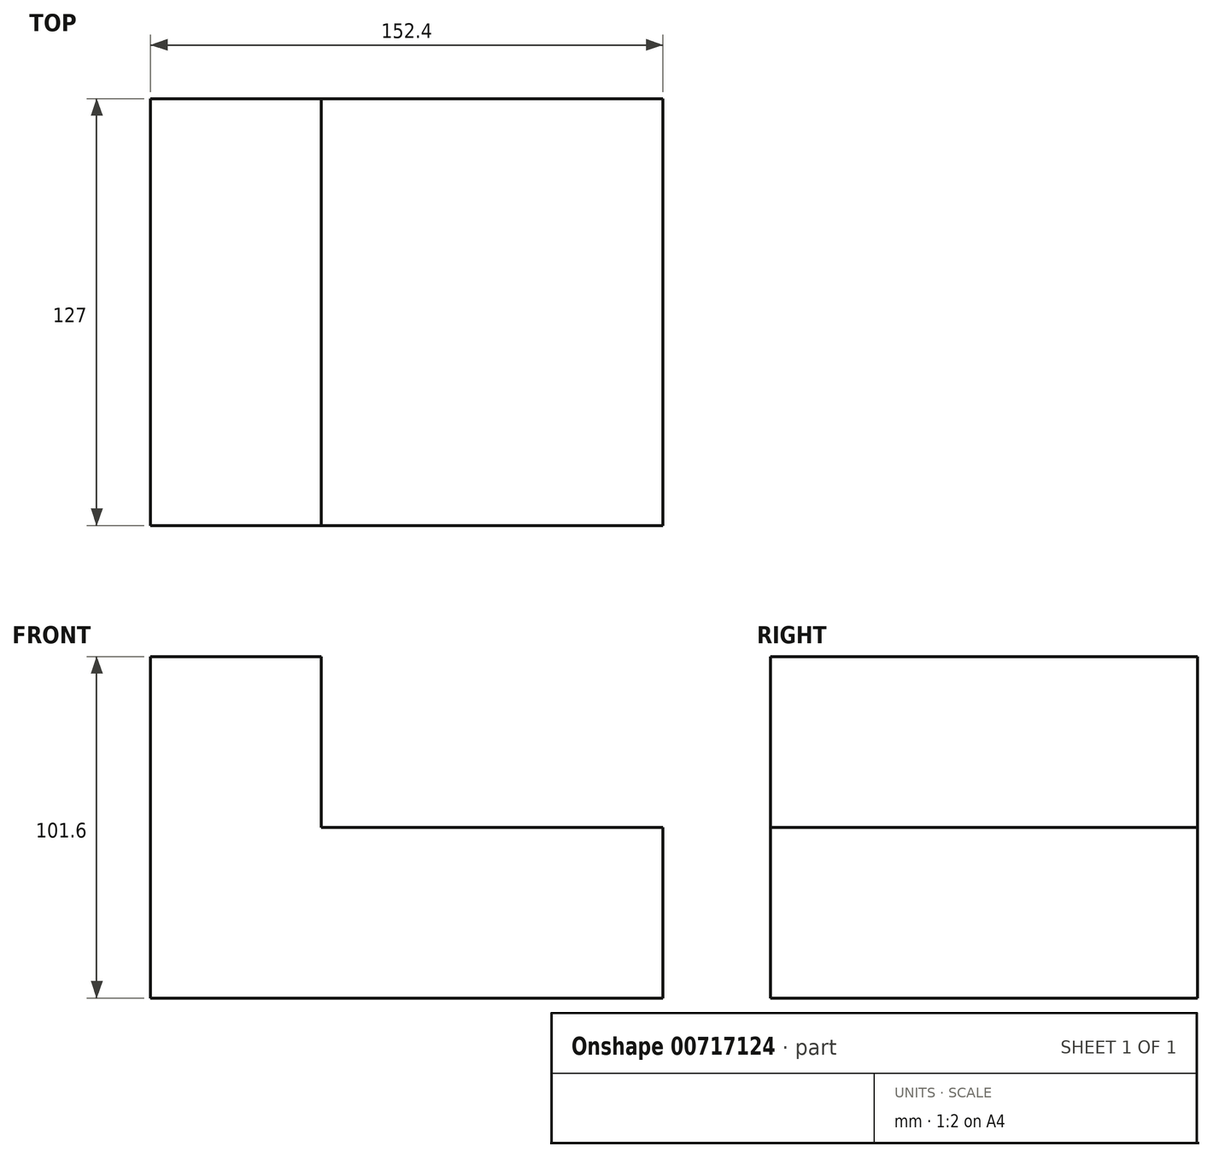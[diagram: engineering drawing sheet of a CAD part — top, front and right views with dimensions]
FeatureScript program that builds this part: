
annotation { "Feature Type Name" : "Feature", "Feature Type Description" : "" }
export const myFeature = defineFeature(function(context is Context, id is Id, definition is map)
    precondition{}
    {
        {
            var Q0;
            Q0=qCreatedBy(makeId("Front.planeOp"),FACE);
            var sketch = newSketch(context, id + "F0", { "sketchPlane" : qUnion([Q0])});
            skLineSegment(sketch, "E0", {"start": v(-145.27, -66.72) * mm, "end": v(7.13, -66.72) * mm});
            skLineSegment(sketch, "E1", {"start": v(7.13, -66.72) * mm, "end": v(7.13, -15.92) * mm});
            skLineSegment(sketch, "E2", {"start": v(7.13, -15.92) * mm, "end": v(-94.47, -15.92) * mm});
            skLineSegment(sketch, "E3", {"start": v(-94.47, -15.92) * mm, "end": v(-94.47, 34.88) * mm});
            skLineSegment(sketch, "E4", {"start": v(-94.47, 34.88) * mm, "end": v(-145.27, 34.88) * mm});
            skLineSegment(sketch, "E5", {"start": v(-145.27, 34.88) * mm, "end": v(-145.27, -66.72) * mm});
            skSolve(sketch);
        }
        {
            var Q0;
            Q0=makeQuery(id+"F0.imprint","IMPRINT",FACE,{"disambiguationData":[TD([[makeQuery(id+"F0.imprint","IMPRINT",EDGE,{"derivedFrom":sQuery(id+"F0.wireOp",EDGE,"E0")}),1.0]])]});
            extrude(context, id + "F1", {"entities" : qUnion([Q0]), "depth" : 127 * mm, "offsetDistance" : 25.4 * mm});
        }
    });
